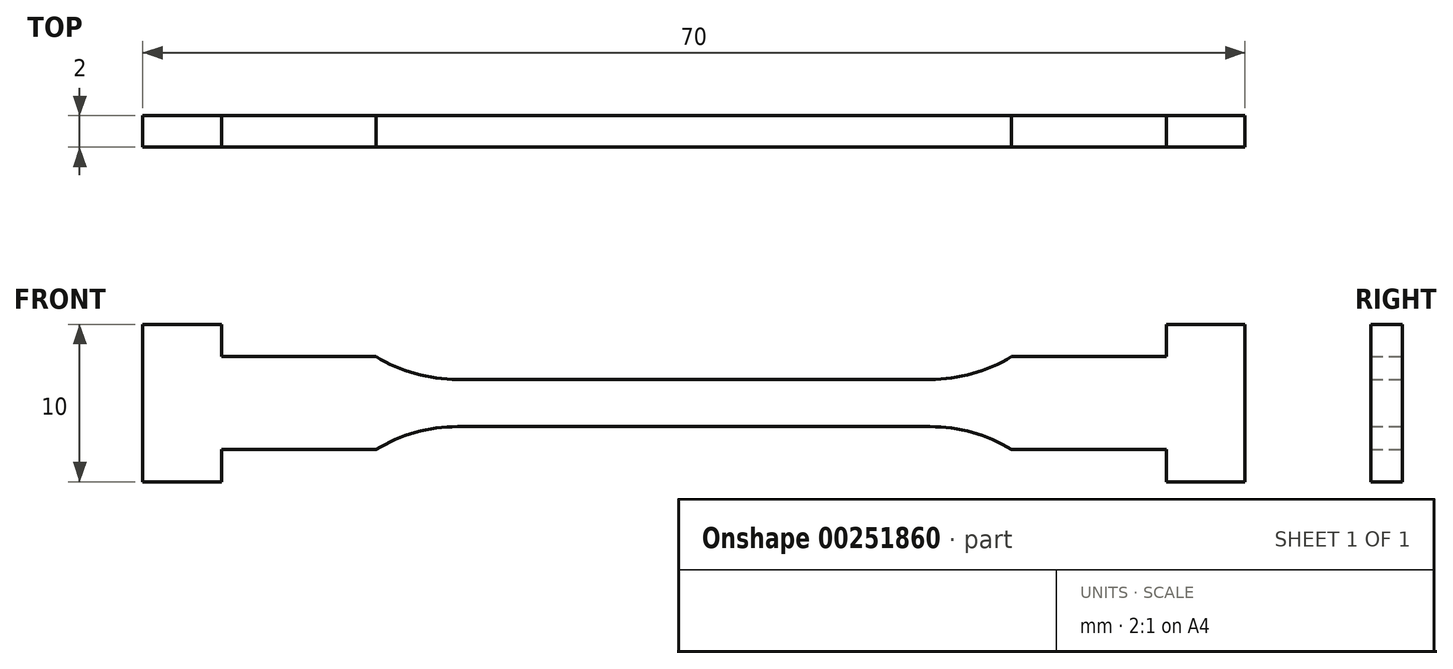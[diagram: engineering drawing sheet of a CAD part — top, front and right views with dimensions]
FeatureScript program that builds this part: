
annotation { "Feature Type Name" : "Feature", "Feature Type Description" : "" }
export const myFeature = defineFeature(function(context is Context, id is Id, definition is map)
    precondition{}
    {
        {
            var Q0;
            Q0=qCreatedBy(makeId("Front.planeOp"),FACE);
            var sketch = newSketch(context, id + "F0", { "sketchPlane" : qUnion([Q0])});
            skLineSegment(sketch, "E0.bottom", {"start": v(35, 5) * mm, "end": v(30, 5) * mm});
            skLineSegment(sketch, "E0.top", {"start": v(35, -5) * mm, "end": v(30, -5) * mm});
            skLineSegment(sketch, "E0.left", {"start": v(35, 5) * mm, "end": v(35, -5) * mm});
            skLineSegment(sketch, "E0.right", {"start": v(-35, 5) * mm, "end": v(-35, -5) * mm});
            skPoint(sketch, "E0.middle", {"position": v(0, 0) * mm});
            skLineSegment(sketch, "E1.left", {"start": v(30, 5) * mm, "end": v(30, 2.95) * mm});
            skLineSegment(sketch, "E1.right", {"start": v(-30, 5) * mm, "end": v(-30, 2.95) * mm});
            skLineSegment(sketch, "E2.bottom", {"start": v(-30, 2.95) * mm, "end": v(-20.19, 2.95) * mm});
            skLineSegment(sketch, "E2.top", {"start": v(-30, -2.95) * mm, "end": v(-20.19, -2.95) * mm});
            skLineSegment(sketch, "E3.bottom", {"start": v(15, 1.5) * mm, "end": v(-15, 1.5) * mm});
            skLineSegment(sketch, "E3.top", {"start": v(15, -1.5) * mm, "end": v(-15, -1.5) * mm});
            skArc(sketch, "E4", {"start": v(-20.19, 2.95) * mm, "mid": v(-17.7, 1.87) * mm, "end": v(-15, 1.5) * mm});
            skArc(sketch, "E5", {"start": v(-15, -1.5) * mm, "mid": v(-17.7, -1.87) * mm, "end": v(-20.19, -2.95) * mm});
            skArc(sketch, "E6", {"start": v(20.19, -2.95) * mm, "mid": v(17.7, -1.87) * mm, "end": v(15, -1.5) * mm});
            skArc(sketch, "E7", {"start": v(15, 1.5) * mm, "mid": v(17.7, 1.87) * mm, "end": v(20.19, 2.95) * mm});
            skLineSegment(sketch, "E8.trimOffspring", {"start": v(-30, 5) * mm, "end": v(-35, 5) * mm});
            skLineSegment(sketch, "E9.trimOffspring", {"start": v(20.19, 2.95) * mm, "end": v(30, 2.95) * mm});
            skLineSegment(sketch, "E10.trimOffspring", {"start": v(-30, -5) * mm, "end": v(-35, -5) * mm});
            skLineSegment(sketch, "E11.trimOffspring", {"start": v(20.19, -2.95) * mm, "end": v(30, -2.95) * mm});
            skLineSegment(sketch, "E12.trimOffspring", {"start": v(30, -2.95) * mm, "end": v(30, -5) * mm});
            skLineSegment(sketch, "E13.trimOffspring", {"start": v(-30, -2.95) * mm, "end": v(-30, -5) * mm});
            skSolve(sketch);
        }
        {
            var Q0;
            Q0=makeQuery(id+"F0.imprint","IMPRINT",FACE,{"disambiguationData":[TD([[makeQuery(id+"F0.imprint","IMPRINT",EDGE,{"derivedFrom":sQuery(id+"F0.wireOp",EDGE,"E0.bottom")}),1.0]])]});
            extrude(context, id + "F1", {"entities" : qUnion([Q0]), "depth" : 2 * mm});
        }
    });
